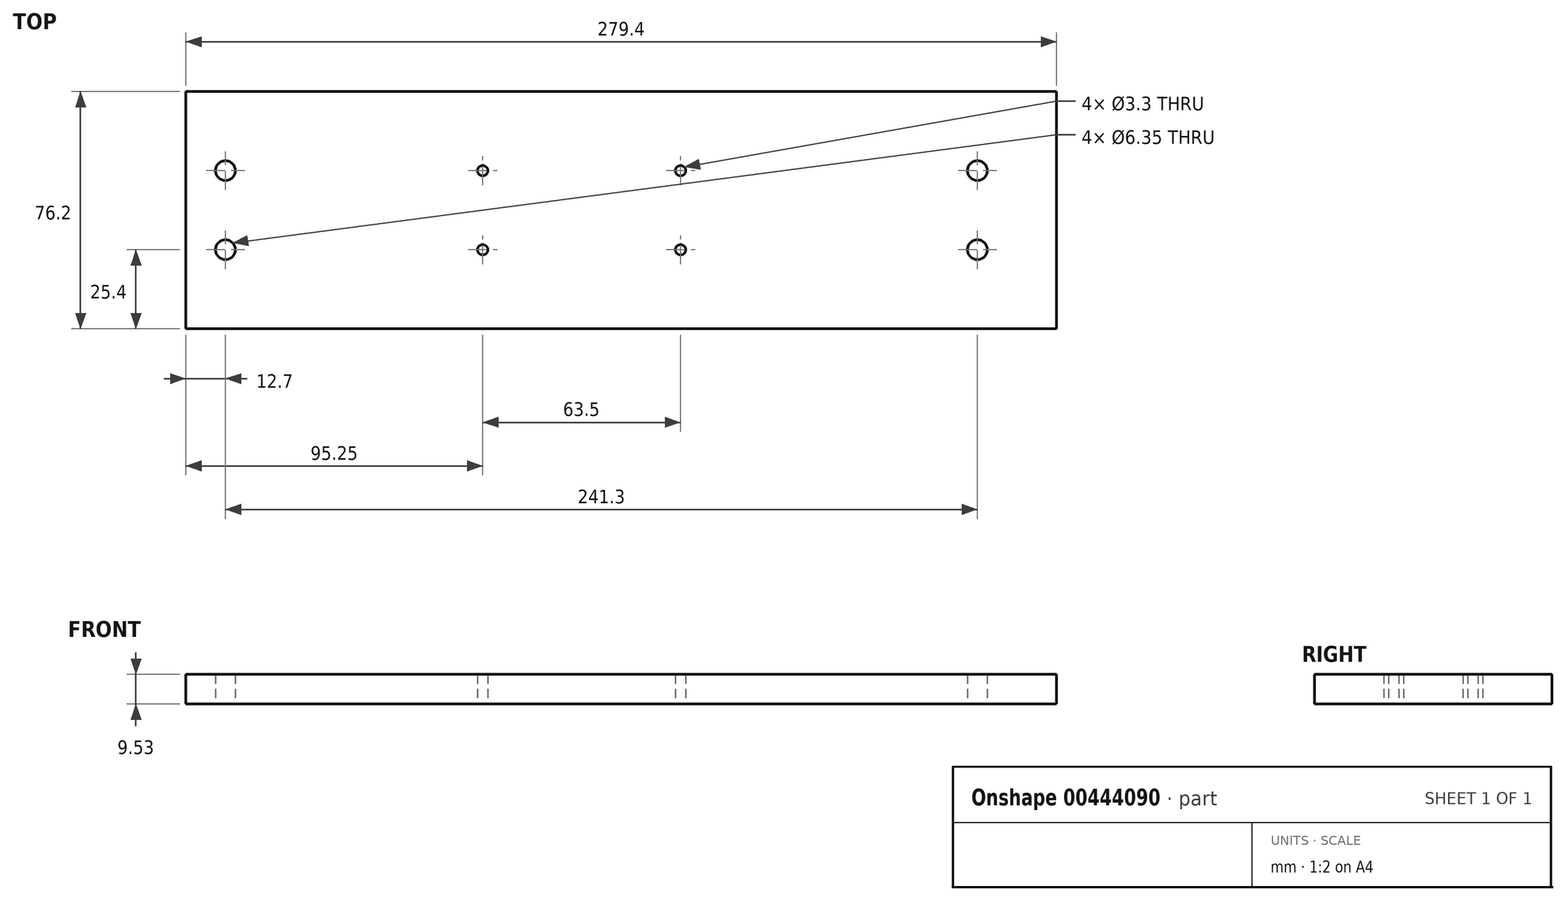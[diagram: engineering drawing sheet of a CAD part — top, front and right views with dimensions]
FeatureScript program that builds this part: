
annotation { "Feature Type Name" : "Feature", "Feature Type Description" : "" }
export const myFeature = defineFeature(function(context is Context, id is Id, definition is map)
    precondition{}
    {
        {
            var Q0;
            Q0=qCreatedBy(makeId("Top.planeOp"),FACE);
            var sketch = newSketch(context, id + "F0", { "sketchPlane" : qUnion([Q0])});
            skLineSegment(sketch, "E0.bottom", {"start": v(-152.4, 38.1) * mm, "end": v(127, 38.1) * mm});
            skLineSegment(sketch, "E0.top", {"start": v(-152.4, -38.1) * mm, "end": v(127, -38.1) * mm});
            skLineSegment(sketch, "E0.left", {"start": v(-152.4, 38.1) * mm, "end": v(-152.4, -38.1) * mm});
            skLineSegment(sketch, "E0.right", {"start": v(127, 38.1) * mm, "end": v(127, -38.1) * mm});
            skLineSegment(sketch, "E1", {"start": v(-139.7, 61.1) * mm, "end": v(-139.7, -92.69) * mm});
            skLineSegment(sketch, "E2", {"start": v(101.6, 74.66) * mm, "end": v(101.6, -81.7) * mm});
            skLineSegment(sketch, "E3", {"start": v(-173.2, 0) * mm, "end": v(211.25, 0) * mm, "construction": true});
            skLineSegment(sketch, "E4", {"start": v(-57.15, 106.97) * mm, "end": v(-57.15, -87.52) * mm});
            skLineSegment(sketch, "E5", {"start": v(6.35, 88.88) * mm, "end": v(6.35, -81.7) * mm});
            skLineSegment(sketch, "E6", {"start": v(-191.32, 12.7) * mm, "end": v(193.18, 12.7) * mm});
            skCircle(sketch, "E7", {"center": v(-139.7, 12.7) * mm, "radius": 3.18 * mm});
            skCircle(sketch, "E8", {"center": v(-57.15, 12.7) * mm, "radius": 1.65 * mm});
            skCircle(sketch, "E9", {"center": v(6.35, 12.7) * mm, "radius": 1.65 * mm});
            skCircle(sketch, "E10", {"center": v(101.6, 12.7) * mm, "radius": 3.18 * mm});
            skCircle(sketch, "E11.MirrorC", {"center": v(101.6, -12.7) * mm, "radius": 3.18 * mm});
            skCircle(sketch, "E12.MirrorC", {"center": v(6.35, -12.7) * mm, "radius": 1.65 * mm});
            skCircle(sketch, "E13.MirrorC", {"center": v(-57.15, -12.7) * mm, "radius": 1.65 * mm});
            skCircle(sketch, "E14.MirrorC", {"center": v(-139.7, -12.7) * mm, "radius": 3.18 * mm});
            skSolve(sketch);
        }
        {
            var Q0;
            Q0 = qSketchRegion(id + "F0", true);
            extrude(context, id + "F1", {"entities" : qUnion([Q0]), "depth" : 9.52 * mm});
        }
    });
